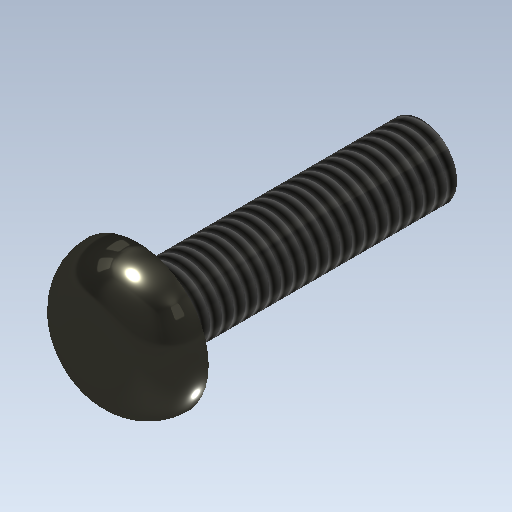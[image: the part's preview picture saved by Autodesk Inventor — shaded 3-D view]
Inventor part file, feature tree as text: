
AUTODESK INVENTOR PART (.ipt)
format: ipt  version: 2020.2 (Build 242310000, 310)  size: 187,392 bytes
history: native  units: mm
features: extrude x5, sketch x5, other x1, fillet x1, thread x1
ambient origin geometry x1: Origin
bodies: Body1 (feature_tree)
feature tree (13):
  other  "ソリッド1"
  extrude  "押し出し1"  Depth=3.0mm
  extrude  "押し出し2"  Depth=6.0mm TaperAngle=0.0deg
  fillet  "フィレット1"  Radius=6.0mm
  thread  "ねじ1"
  extrude  "押し出し3"  Depth=2.0mm TaperAngle=0.0deg
  extrude  "押し出し4"  Depth=2.0mm
  extrude  "押し出し5"  Depth=10.0mm TaperAngle=0.0deg
  sketch  "スケッチ1"
  sketch  "スケッチ2"
  sketch  "スケッチ3"
  sketch  "スケッチ4"
  sketch  "スケッチ5"
